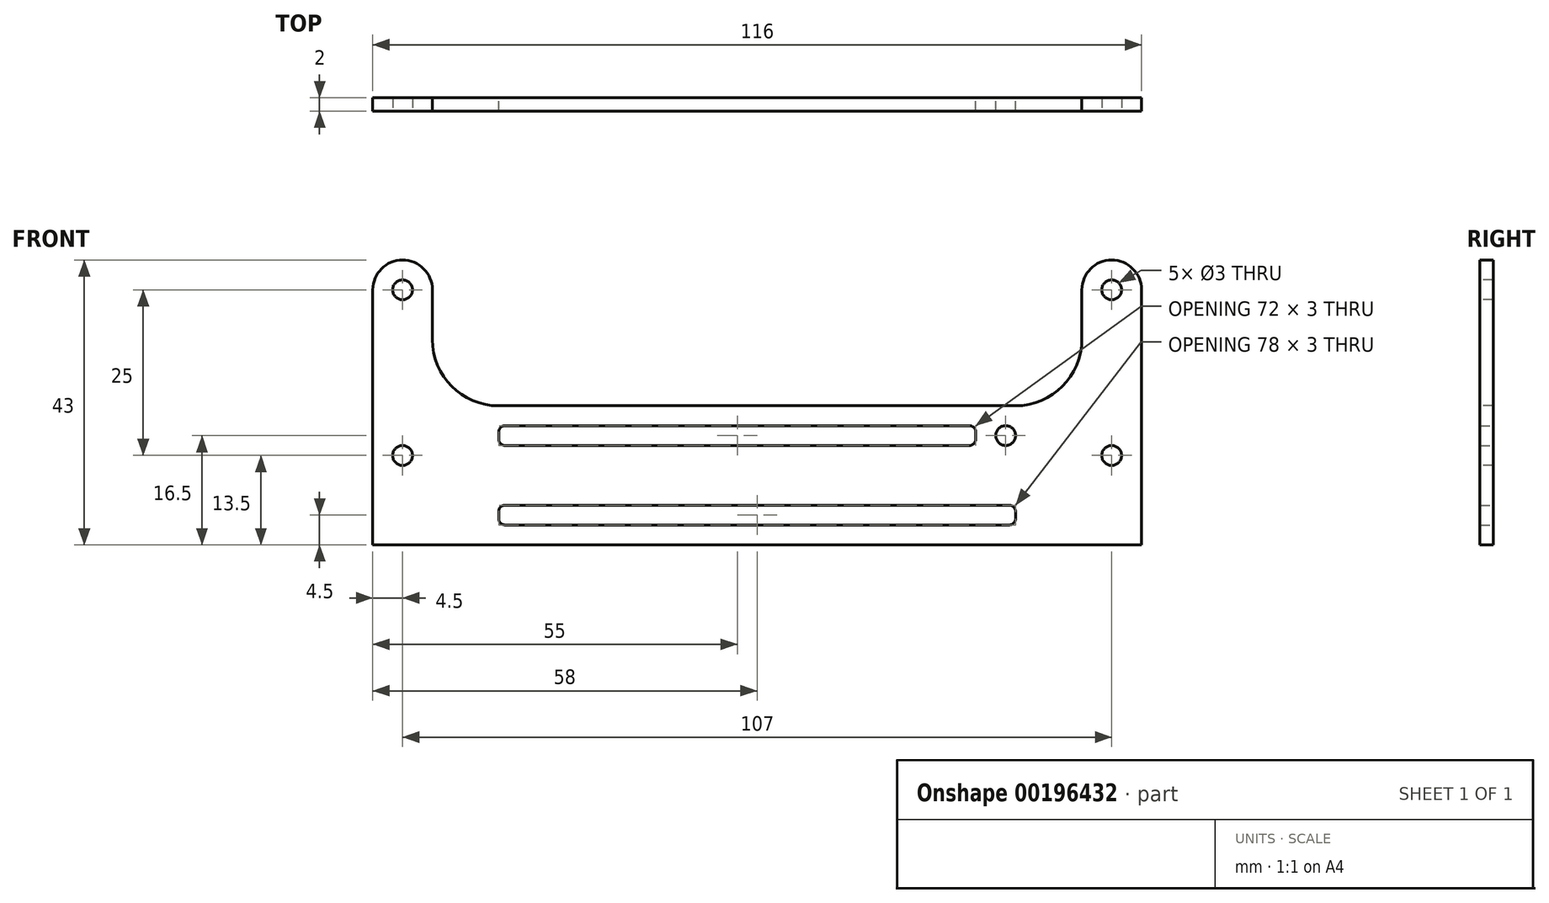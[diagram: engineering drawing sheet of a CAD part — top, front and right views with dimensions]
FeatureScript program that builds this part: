
annotation { "Feature Type Name" : "Feature", "Feature Type Description" : "" }
export const myFeature = defineFeature(function(context is Context, id is Id, definition is map)
    precondition{}
    {
        {
            var Q0;
            Q0=qCreatedBy(makeId("Front.planeOp"),FACE);
            var sketch = newSketch(context, id + "F0", { "sketchPlane" : qUnion([Q0])});
            skLineSegment(sketch, "E0.bottom", {"start": v(42, 10.5) * mm, "end": v(-42, 10.5) * mm});
            skLineSegment(sketch, "E0.top", {"start": v(42, -10.5) * mm, "end": v(-42, -10.5) * mm});
            skLineSegment(sketch, "E0.left", {"start": v(42, 10.5) * mm, "end": v(42, -10.5) * mm});
            skLineSegment(sketch, "E0.right", {"start": v(-42, 10.5) * mm, "end": v(-42, -10.5) * mm});
            skPoint(sketch, "E0.middle", {"position": v(0, 0) * mm});
            skLineSegment(sketch, "E1.bottom", {"start": v(39, -4.5) * mm, "end": v(-39, -4.5) * mm});
            skLineSegment(sketch, "E1.top", {"start": v(39, -7.5) * mm, "end": v(-39, -7.5) * mm});
            skLineSegment(sketch, "E1.left", {"start": v(39, -4.5) * mm, "end": v(39, -7.5) * mm});
            skLineSegment(sketch, "E1.right", {"start": v(-39, -4.5) * mm, "end": v(-39, -7.5) * mm});
            skPoint(sketch, "E1.middle", {"position": v(0, -6) * mm});
            skLineSegment(sketch, "E2.bottom", {"start": v(39, 1.5) * mm, "end": v(-39, 1.5) * mm, "construction": true});
            skLineSegment(sketch, "E2.top", {"start": v(39, -1.5) * mm, "end": v(-39, -1.5) * mm, "construction": true});
            skLineSegment(sketch, "E2.left", {"start": v(39, 1.5) * mm, "end": v(39, -1.5) * mm, "construction": true});
            skLineSegment(sketch, "E2.right", {"start": v(-39, 1.5) * mm, "end": v(-39, -1.5) * mm, "construction": true});
            skLineSegment(sketch, "E3.bottom", {"start": v(-39, 7.5) * mm, "end": v(33, 7.5) * mm});
            skLineSegment(sketch, "E3.top", {"start": v(-39, 4.5) * mm, "end": v(33, 4.5) * mm});
            skLineSegment(sketch, "E3.left", {"start": v(-39, 7.5) * mm, "end": v(-39, 4.5) * mm});
            skLineSegment(sketch, "E3.right", {"start": v(33, 7.5) * mm, "end": v(33, 4.5) * mm});
            skCircle(sketch, "E4", {"center": v(37.5, 6) * mm, "radius": 1.5 * mm});
            skLineSegment(sketch, "E5", {"start": v(0, 0) * mm, "end": v(0, 10.5) * mm, "construction": true});
            skSolve(sketch);
        }
        {
            var Q0;
            Q0=qSketchRegion(id+"F0",true);
            extrude(context, id + "F1", {"entities" : qUnion([Q0]), "depth" : 2 * mm});
        }
        {
            var Q0;
            Q0=makeQuery(id+"F1.opExtrude","SWEPT_EDGE",EDGE,{"disambiguationData":[OSD([sQuery(id+"F0.wireOp",EDGE,"E3.bottom"),sQuery(id+"F0.wireOp",EDGE,"E3.left")])]});
            var Q1;
            Q1=makeQuery(id+"F1.opExtrude","SWEPT_EDGE",EDGE,{"disambiguationData":[OSD([sQuery(id+"F0.wireOp",EDGE,"E2.bottom"),sQuery(id+"F0.wireOp",EDGE,"E2.right")])]});
            var Q2;
            Q2=makeQuery(id+"F1.opExtrude","SWEPT_EDGE",EDGE,{"disambiguationData":[OSD([sQuery(id+"F0.wireOp",EDGE,"E1.bottom"),sQuery(id+"F0.wireOp",EDGE,"E1.right")])]});
            var Q3;
            Q3=makeQuery(id+"F1.opExtrude","SWEPT_EDGE",EDGE,{"disambiguationData":[OSD([sQuery(id+"F0.wireOp",EDGE,"E3.top"),sQuery(id+"F0.wireOp",EDGE,"E3.left")])]});
            var Q4;
            Q4=makeQuery(id+"F1.opExtrude","SWEPT_EDGE",EDGE,{"disambiguationData":[OSD([sQuery(id+"F0.wireOp",EDGE,"E2.top"),sQuery(id+"F0.wireOp",EDGE,"E2.right")])]});
            var Q5;
            Q5=makeQuery(id+"F1.opExtrude","SWEPT_EDGE",EDGE,{"disambiguationData":[OSD([sQuery(id+"F0.wireOp",EDGE,"E1.top"),sQuery(id+"F0.wireOp",EDGE,"E1.right")])]});
            var Q6;
            Q6=makeQuery(id+"F1.opExtrude","SWEPT_EDGE",EDGE,{"disambiguationData":[OSD([sQuery(id+"F0.wireOp",EDGE,"E3.bottom"),sQuery(id+"F0.wireOp",EDGE,"E3.right")])]});
            var Q7;
            Q7=makeQuery(id+"F1.opExtrude","SWEPT_EDGE",EDGE,{"disambiguationData":[OSD([sQuery(id+"F0.wireOp",EDGE,"E2.bottom"),sQuery(id+"F0.wireOp",EDGE,"E2.left")])]});
            var Q8;
            Q8=makeQuery(id+"F1.opExtrude","SWEPT_EDGE",EDGE,{"disambiguationData":[OSD([sQuery(id+"F0.wireOp",EDGE,"E1.bottom"),sQuery(id+"F0.wireOp",EDGE,"E1.left")])]});
            var Q9;
            Q9=makeQuery(id+"F1.opExtrude","SWEPT_EDGE",EDGE,{"disambiguationData":[OSD([sQuery(id+"F0.wireOp",EDGE,"E1.top"),sQuery(id+"F0.wireOp",EDGE,"E1.left")])]});
            var Q10;
            Q10=makeQuery(id+"F1.opExtrude","SWEPT_EDGE",EDGE,{"disambiguationData":[OSD([sQuery(id+"F0.wireOp",EDGE,"E2.top"),sQuery(id+"F0.wireOp",EDGE,"E2.left")])]});
            var Q11;
            Q11=makeQuery(id+"F1.opExtrude","SWEPT_EDGE",EDGE,{"disambiguationData":[OSD([sQuery(id+"F0.wireOp",EDGE,"E3.top"),sQuery(id+"F0.wireOp",EDGE,"E3.right")])]});
            fillet(context, id + "F2", {"entities" : qUnion([Q0, Q1, Q2, Q3, Q4, Q5, Q6, Q7, Q8, Q9, Q10, Q11]), "radius" : 1 * mm, "tangentPropagation" : true, "allowEdgeOverflow" : false});
        }
        {
            var Q0;
            Q0=makeQuery(id+"F1.opExtrude","CAP_FACE",FACE,{"disambiguationData":[OSD([sQuery(id+"F0.wireOp",EDGE,"E0.bottom"),sQuery(id+"F0.wireOp",EDGE,"E0.top"),sQuery(id+"F0.wireOp",EDGE,"E0.left"),sQuery(id+"F0.wireOp",EDGE,"E0.right"),sQuery(id+"F0.wireOp",EDGE,"E1.bottom"),sQuery(id+"F0.wireOp",EDGE,"E1.top"),sQuery(id+"F0.wireOp",EDGE,"E1.left"),sQuery(id+"F0.wireOp",EDGE,"E1.right"),sQuery(id+"F0.wireOp",EDGE,"E2.bottom"),sQuery(id+"F0.wireOp",EDGE,"E2.top"),sQuery(id+"F0.wireOp",EDGE,"E2.left"),sQuery(id+"F0.wireOp",EDGE,"E2.right"),sQuery(id+"F0.wireOp",EDGE,"E3.bottom"),sQuery(id+"F0.wireOp",EDGE,"E3.top"),sQuery(id+"F0.wireOp",EDGE,"E3.left"),sQuery(id+"F0.wireOp",EDGE,"E3.right"),sQuery(id+"F0.wireOp",EDGE,"E4")])],"isStart":false});
            var sketch = newSketch(context, id + "F3", { "sketchPlane" : qUnion([Q0])});
            skLineSegment(sketch, "E6.bottom", {"start": v(53.5, 0) * mm, "end": v(-53.5, 0) * mm});
            skLineSegment(sketch, "E6.top", {"start": v(53.5, 0) * mm, "end": v(-53.5, 0) * mm, "construction": true});
            skLineSegment(sketch, "E6.left", {"start": v(53.5, 0) * mm, "end": v(53.5, 0) * mm});
            skLineSegment(sketch, "E6.right", {"start": v(-53.5, 0) * mm, "end": v(-53.5, 0) * mm});
            skPoint(sketch, "E6.middle", {"position": v(0, 0) * mm});
            skLineSegment(sketch, "E7", {"start": v(37.5, 6) * mm, "end": v(53.5, 6) * mm, "construction": true});
            skLineSegment(sketch, "E8", {"start": v(53.5, 6) * mm, "end": v(53.5, 3) * mm, "construction": true});
            skCircle(sketch, "E9", {"center": v(53.5, 3) * mm, "radius": 1.5 * mm});
            skLineSegment(sketch, "E10", {"start": v(53.5, 3) * mm, "end": v(53.5, 28) * mm, "construction": true});
            skCircle(sketch, "E11", {"center": v(53.5, 28) * mm, "radius": 1.5 * mm});
            skLineSegment(sketch, "E12.bottom", {"start": v(42, -10.5) * mm, "end": v(58, -10.5) * mm});
            skLineSegment(sketch, "E12.top", {"start": v(49, 32.5) * mm, "end": v(58, 32.5) * mm});
            skLineSegment(sketch, "E12.left", {"start": v(42, -10.5) * mm, "end": v(42, 10.5) * mm});
            skLineSegment(sketch, "E12.right", {"start": v(58, -10.5) * mm, "end": v(58, 32.5) * mm});
            skLineSegment(sketch, "E13.top", {"start": v(42, 10.5) * mm, "end": v(49, 10.5) * mm});
            skLineSegment(sketch, "E13.right", {"start": v(49, 32.5) * mm, "end": v(49, 10.5) * mm});
            skLineSegment(sketch, "E14.MirrorCS", {"start": v(-53.5, 6) * mm, "end": v(-53.5, 3) * mm, "construction": true});
            skLineSegment(sketch, "E15.MirrorCS", {"start": v(-53.5, 0) * mm, "end": v(53.5, 0) * mm});
            skLineSegment(sketch, "E16.MirrorCS", {"start": v(-49, 32.5) * mm, "end": v(-49, 10.5) * mm});
            skLineSegment(sketch, "E17.MirrorCS", {"start": v(-42, -10.5) * mm, "end": v(-58, -10.5) * mm});
            skLineSegment(sketch, "E18.MirrorCS", {"start": v(-53.5, 0) * mm, "end": v(53.5, 0) * mm, "construction": true});
            skLineSegment(sketch, "E19.MirrorCS", {"start": v(-58, -10.5) * mm, "end": v(-58, 32.5) * mm});
            skLineSegment(sketch, "E20.MirrorCS", {"start": v(-53.5, 3) * mm, "end": v(-53.5, 28) * mm, "construction": true});
            skCircle(sketch, "E21.MirrorC", {"center": v(-53.5, 28) * mm, "radius": 1.5 * mm});
            skCircle(sketch, "E22.MirrorC", {"center": v(-53.5, 3) * mm, "radius": 1.5 * mm});
            skLineSegment(sketch, "E23.MirrorCS", {"start": v(-37.5, 6) * mm, "end": v(-53.5, 6) * mm, "construction": true});
            skLineSegment(sketch, "E24.MirrorCS", {"start": v(-42, -10.5) * mm, "end": v(-42, 10.5) * mm});
            skLineSegment(sketch, "E25.MirrorCS", {"start": v(-42, 10.5) * mm, "end": v(-49, 10.5) * mm});
            skLineSegment(sketch, "E26.MirrorCS", {"start": v(-49, 32.5) * mm, "end": v(-58, 32.5) * mm});
            skSolve(sketch);
        }
        {
            var Q0;
            Q0 = qSketchRegion(id + "F3", true);
            extrude(context, id + "F4", {"entities" : qUnion([Q0]), "operationType" : NewBodyOperationType.ADD, "oppositeDirection" : true, "depth" : 2 * mm});
        }
        {
            var Q0;
            Q0=makeQuery(id+"F4.opExtrude","SWEPT_EDGE",EDGE,{"disambiguationData":[OSD([sQuery(id+"F3.wireOp",EDGE,"E16.MirrorCS"),sQuery(id+"F3.wireOp",EDGE,"E25.MirrorCS")])]});
            var Q1;
            Q1=makeQuery(id+"F4.opExtrude","SWEPT_EDGE",EDGE,{"disambiguationData":[OSD([sQuery(id+"F3.wireOp",EDGE,"E13.top"),sQuery(id+"F3.wireOp",EDGE,"E13.right")])]});
            fillet(context, id + "F5", {"entities" : qUnion([Q0, Q1]), "radius" : 10 * mm, "tangentPropagation" : true, "allowEdgeOverflow" : false});
        }
        {
            var Q0;
            Q0=makeQuery(id+"F4.opExtrude","SWEPT_EDGE",EDGE,{"disambiguationData":[OSD([sQuery(id+"F3.wireOp",EDGE,"E16.MirrorCS"),sQuery(id+"F3.wireOp",EDGE,"E26.MirrorCS")])]});
            var Q1;
            Q1=makeQuery(id+"F4.opExtrude","SWEPT_EDGE",EDGE,{"disambiguationData":[OSD([sQuery(id+"F3.wireOp",EDGE,"E19.MirrorCS"),sQuery(id+"F3.wireOp",EDGE,"E26.MirrorCS")])]});
            var Q2;
            Q2=makeQuery(id+"F4.opExtrude","SWEPT_EDGE",EDGE,{"disambiguationData":[OSD([sQuery(id+"F3.wireOp",EDGE,"E12.top"),sQuery(id+"F3.wireOp",EDGE,"E12.right")])]});
            var Q3;
            Q3=makeQuery(id+"F4.opExtrude","SWEPT_EDGE",EDGE,{"disambiguationData":[OSD([sQuery(id+"F3.wireOp",EDGE,"E12.top"),sQuery(id+"F3.wireOp",EDGE,"E13.right")])]});
            fillet(context, id + "F6", {"entities" : qUnion([Q0, Q1, Q2, Q3]), "radius" : 4.5 * mm, "tangentPropagation" : true, "allowEdgeOverflow" : false});
        }
    });
